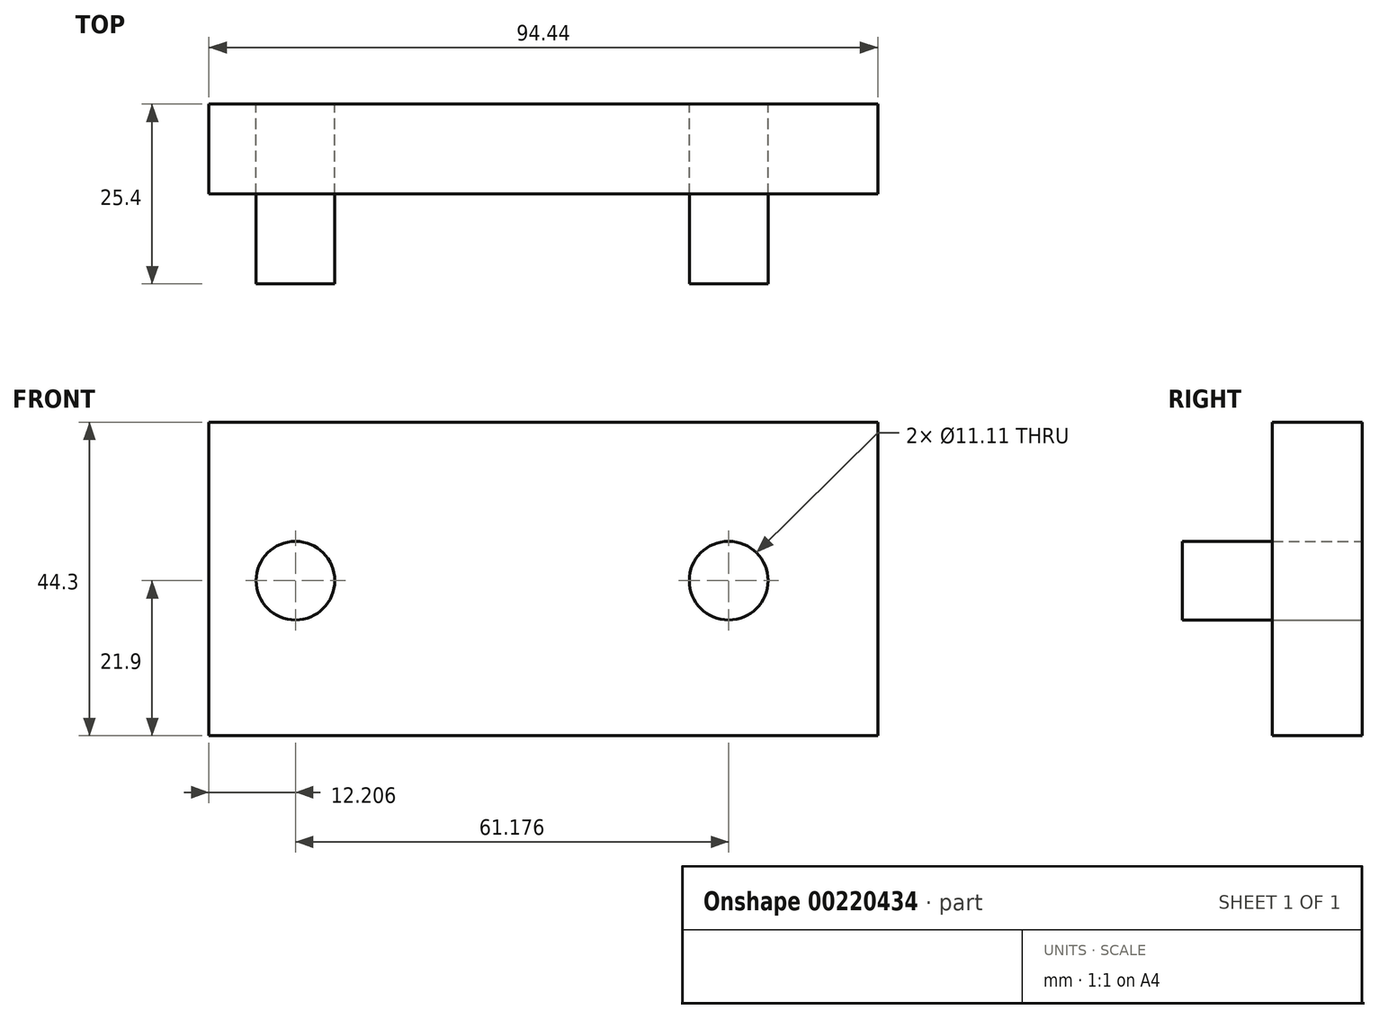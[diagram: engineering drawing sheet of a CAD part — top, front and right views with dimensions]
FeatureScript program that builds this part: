
annotation { "Feature Type Name" : "Feature", "Feature Type Description" : "" }
export const myFeature = defineFeature(function(context is Context, id is Id, definition is map)
    precondition{}
    {
        {
            var Q0;
            Q0=qCreatedBy(makeId("Front.planeOp"),FACE);
            var sketch = newSketch(context, id + "F0", { "sketchPlane" : qUnion([Q0])});
            skLineSegment(sketch, "E0.bottom", {"start": v(-43.63, 22.4) * mm, "end": v(50.81, 22.4) * mm});
            skLineSegment(sketch, "E0.top", {"start": v(-43.63, -21.9) * mm, "end": v(50.81, -21.9) * mm});
            skLineSegment(sketch, "E0.left", {"start": v(-43.63, 22.4) * mm, "end": v(-43.63, -21.9) * mm});
            skLineSegment(sketch, "E0.right", {"start": v(50.81, 22.4) * mm, "end": v(50.81, -21.9) * mm});
            skCircle(sketch, "E1", {"center": v(-31.42, 0) * mm, "radius": 5.56 * mm});
            skCircle(sketch, "E2", {"center": v(29.75, 0) * mm, "radius": 5.56 * mm});
            skSolve(sketch);
        }
        {
            var Q0;
            Q0=qCreatedBy(makeId("Front.planeOp"),FACE);
            var sketch = newSketch(context, id + "F1", { "sketchPlane" : qUnion([Q0])});
            skSolve(sketch);
        }
        {
            var Q0;
            Q0 = qSketchRegion(id + "F1", true);
            var Q1;
            Q1=makeQuery(id+"F0.imprint","IMPRINT",FACE,{"disambiguationData":[TD([[makeQuery(id+"F0.imprint","IMPRINT",EDGE,{"derivedFrom":sQuery(id+"F0.wireOp",EDGE,"E2")}),1.0]])]});
            var Q2;
            Q2=makeQuery(id+"F0.imprint","IMPRINT",FACE,{"disambiguationData":[TD([[makeQuery(id+"F0.imprint","IMPRINT",EDGE,{"derivedFrom":sQuery(id+"F0.wireOp",EDGE,"E1")}),1.0]])]});
            extrude(context, id + "F2", {"entities" : qUnion([Q0, Q1, Q2]), "depth" : 25.4 * mm});
        }
        {
            var Q0;
            Q0 = qSketchRegion(id + "F0", true);
            extrude(context, id + "F3", {"entities" : qUnion([Q0]), "depth" : 12.7 * mm});
        }
    });
